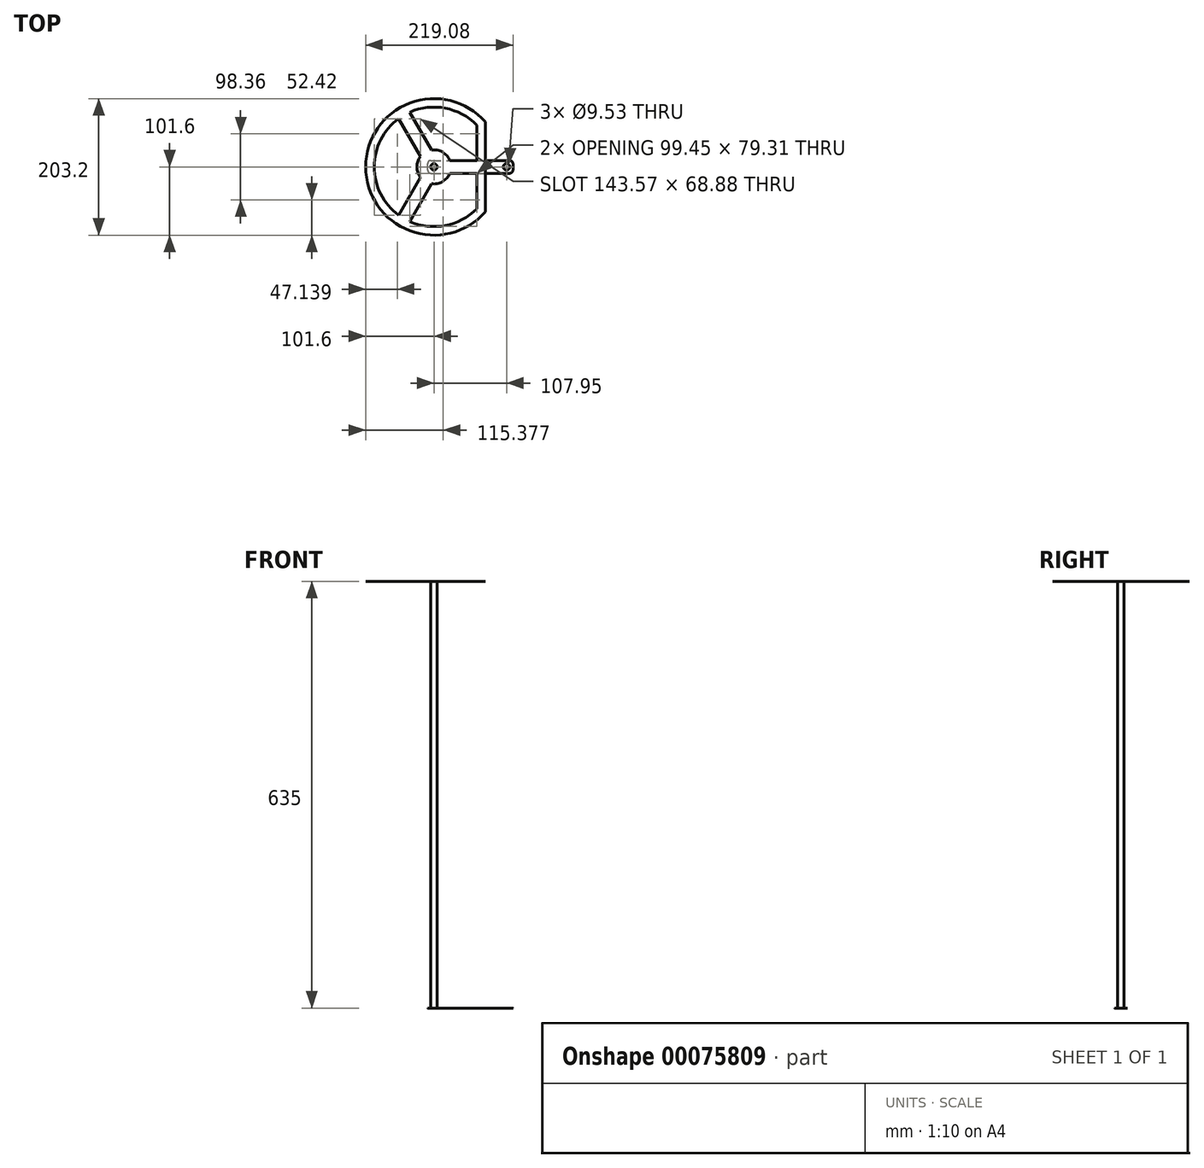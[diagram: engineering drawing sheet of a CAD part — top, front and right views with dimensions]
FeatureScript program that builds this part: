
annotation { "Feature Type Name" : "Feature", "Feature Type Description" : "" }
export const myFeature = defineFeature(function(context is Context, id is Id, definition is map)
    precondition{}
    {
        {
            var Q0;
            Q0=qCreatedBy(makeId("Top.planeOp"),FACE);
            var sketch = newSketch(context, id + "F0", { "sketchPlane" : qUnion([Q0])});
            skCircle(sketch, "E0", {"center": v(0, 0) * mm, "radius": 4.76 * mm});
            skSolve(sketch);
        }
        {
            var Q0;
            Q0 = qSketchRegion(id + "F0", true);
            extrude(context, id + "F1", {"entities" : qUnion([Q0]), "oppositeDirection" : true, "depth" : 635 * mm});
        }
        {
            var Q0;
            Q0=makeQuery(id+"F1.opExtrude","CAP_FACE",FACE,{"disambiguationData":[OSD([sQuery(id+"F0.wireOp",EDGE,"E0")])],"isStart":false});
            var sketch = newSketch(context, id + "F2", { "sketchPlane" : qUnion([Q0])});
            skLineSegment(sketch, "E1.bottom", {"start": v(-9.53, 9.52) * mm, "end": v(117.47, 9.52) * mm});
            skLineSegment(sketch, "E1.top", {"start": v(-9.53, -9.53) * mm, "end": v(117.47, -9.53) * mm});
            skLineSegment(sketch, "E1.left", {"start": v(-9.53, 9.52) * mm, "end": v(-9.53, -9.53) * mm});
            skLineSegment(sketch, "E1.right", {"start": v(117.47, 9.52) * mm, "end": v(117.47, -9.53) * mm});
            skCircle(sketch, "E2.0", {"center": v(0, 0) * mm, "radius": 4.76 * mm});
            skLineSegment(sketch, "E3", {"start": v(53.97, 9.52) * mm, "end": v(53.97, -9.53) * mm, "construction": true});
            skCircle(sketch, "E4.MirrorC", {"center": v(107.95, 0) * mm, "radius": 4.76 * mm});
            skSolve(sketch);
        }
        {
            var Q0;
            Q0 = qSketchRegion(id + "F2", true);
            extrude(context, id + "F3", {"entities" : qUnion([Q0]), "oppositeDirection" : true, "depth" : 3 / 203.2 * mm});
        }
        {
            var Q0;
            Q0=makeQuery(id+"F3.opExtrude","SWEPT_EDGE",EDGE,{"disambiguationData":[OSD([sQuery(id+"F2.wireOp",EDGE,"E1.bottom"),sQuery(id+"F2.wireOp",EDGE,"E1.right")])]});
            var Q1;
            Q1=makeQuery(id+"F3.opExtrude","SWEPT_EDGE",EDGE,{"disambiguationData":[OSD([sQuery(id+"F2.wireOp",EDGE,"E1.top"),sQuery(id+"F2.wireOp",EDGE,"E1.right")])]});
            var Q2;
            Q2=makeQuery(id+"F3.opExtrude","SWEPT_EDGE",EDGE,{"disambiguationData":[OSD([sQuery(id+"F2.wireOp",EDGE,"E1.bottom"),sQuery(id+"F2.wireOp",EDGE,"E1.left")])]});
            var Q3;
            Q3=makeQuery(id+"F3.opExtrude","SWEPT_EDGE",EDGE,{"disambiguationData":[OSD([sQuery(id+"F2.wireOp",EDGE,"E1.top"),sQuery(id+"F2.wireOp",EDGE,"E1.left")])]});
            fillet(context, id + "F4", {"entities" : qUnion([Q0, Q1, Q2, Q3]), "radius" : 5 * mm, "tangentPropagation" : true, "allowEdgeOverflow" : false});
        }
        {
            var Q0;
            Q0=qCreatedBy(makeId("Top.planeOp"),FACE);
            var sketch = newSketch(context, id + "F5", { "sketchPlane" : qUnion([Q0])});
            skCircle(sketch, "E5.0", {"center": v(0, 0) * mm, "radius": 4.76 * mm});
            skArc(sketch, "E6", {"start": v(76.2, 67.2) * mm, "mid": v(-101.6, 0) * mm, "end": v(76.2, -67.2) * mm});
            skLineSegment(sketch, "E7", {"start": v(76.2, 67.2) * mm, "end": v(76.2, -67.2) * mm});
            skArc(sketch, "E8.0", {"start": v(63.5, 62.22) * mm, "mid": v(16.76, 87.3) * mm, "end": v(-35.95, 81.3) * mm});
            skLineSegment(sketch, "E8.1", {"start": v(63.5, 62.22) * mm, "end": v(63.5, 9.52) * mm});
            skArc(sketch, "E9", {"start": v(23.55, 9.53) * mm, "mid": v(12.7, 22) * mm, "end": v(-3.52, 25.15) * mm});
            skLineSegment(sketch, "E10", {"start": v(63.5, 9.52) * mm, "end": v(23.55, 9.52) * mm});
            skLineSegment(sketch, "E11", {"start": v(63.5, -9.53) * mm, "end": v(23.55, -9.53) * mm});
            skLineSegment(sketch, "E12.trimOffspring", {"start": v(63.5, -9.53) * mm, "end": v(63.5, -62.22) * mm});
            skLineSegment(sketch, "E13", {"start": v(-3.52, 25.15) * mm, "end": v(-35.95, 81.3) * mm});
            skLineSegment(sketch, "E14", {"start": v(-20.02, 15.63) * mm, "end": v(-52.44, 71.78) * mm});
            skArc(sketch, "E15.trimOffspring", {"start": v(-52.44, 71.78) * mm, "mid": v(-88.9, 0) * mm, "end": v(-52.44, -71.78) * mm});
            skArc(sketch, "E16.trimOffspring", {"start": v(-20.02, 15.63) * mm, "mid": v(-25.4, 0) * mm, "end": v(-20.02, -15.63) * mm});
            skLineSegment(sketch, "E17", {"start": v(-20.02, -15.63) * mm, "end": v(-52.44, -71.78) * mm});
            skLineSegment(sketch, "E18", {"start": v(-3.52, -25.15) * mm, "end": v(-35.95, -81.3) * mm});
            skArc(sketch, "E19.trimOffspring", {"start": v(-3.52, -25.15) * mm, "mid": v(12.7, -22) * mm, "end": v(23.55, -9.53) * mm});
            skArc(sketch, "E20.trimOffspring", {"start": v(-35.95, -81.3) * mm, "mid": v(16.76, -87.3) * mm, "end": v(63.5, -62.22) * mm});
            skSolve(sketch);
        }
        {
            var Q0;
            Q0 = qSketchRegion(id + "F5", true);
            extrude(context, id + "F6", {"entities" : qUnion([Q0]), "oppositeDirection" : true, "depth" : 1 / 203.2 * mm});
        }
    });
